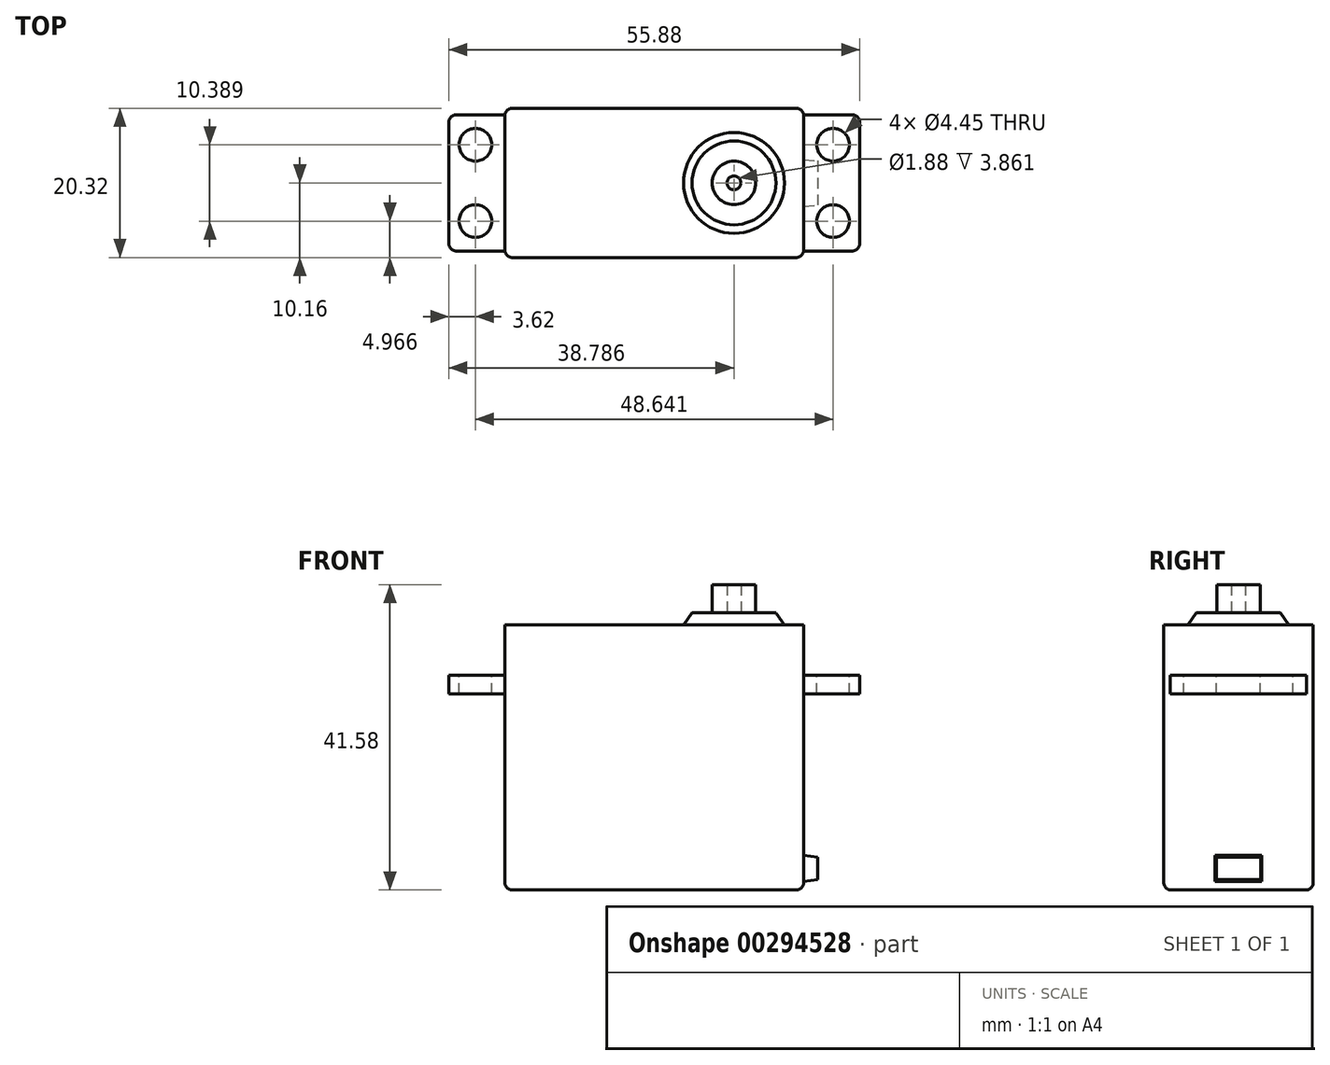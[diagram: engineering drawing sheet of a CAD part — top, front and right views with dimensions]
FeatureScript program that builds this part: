
annotation { "Feature Type Name" : "Feature", "Feature Type Description" : "" }
export const myFeature = defineFeature(function(context is Context, id is Id, definition is map)
    precondition{}
    {
        {
            var Q0;
            Q0=qCreatedBy(makeId("Top.planeOp"),FACE);
            var sketch = newSketch(context, id + "F0", { "sketchPlane" : qUnion([Q0])});
            skLineSegment(sketch, "E0.bottom", {"start": v(20.32, 10.16) * mm, "end": v(-20.32, 10.16) * mm});
            skLineSegment(sketch, "E0.top", {"start": v(20.32, -10.16) * mm, "end": v(-20.32, -10.16) * mm});
            skLineSegment(sketch, "E0.left", {"start": v(20.32, 10.16) * mm, "end": v(20.32, -10.16) * mm});
            skLineSegment(sketch, "E0.right", {"start": v(-20.32, 10.16) * mm, "end": v(-20.32, -10.16) * mm});
            skPoint(sketch, "E0.middle", {"position": v(0, 0) * mm});
            skSolve(sketch);
        }
        {
            var Q0;
            Q0=qSketchRegion(id+"F0",true);
            extrude(context, id + "F1", {"entities" : qUnion([Q0]), "depth" : 36.07 * mm});
        }
        {
            var Q0;
            Q0=makeQuery(id+"F1.opExtrude","SWEPT_FACE",FACE,{"disambiguationData":[OSD([sQuery(id+"F0.wireOp",EDGE,"E0.left")])]});
            var sketch = newSketch(context, id + "F2", { "sketchPlane" : qUnion([Q0])});
            skLineSegment(sketch, "E1.bottom", {"start": v(3.18, 4.75) * mm, "end": v(-3.17, 4.75) * mm});
            skLineSegment(sketch, "E1.top", {"start": v(3.18, 1.14) * mm, "end": v(-3.17, 1.14) * mm});
            skLineSegment(sketch, "E1.left", {"start": v(3.18, 4.75) * mm, "end": v(3.18, 1.14) * mm});
            skLineSegment(sketch, "E1.right", {"start": v(-3.17, 4.75) * mm, "end": v(-3.17, 1.14) * mm});
            skPoint(sketch, "E1.middle", {"position": v(0, 2.95) * mm});
            skSolve(sketch);
        }
        {
            var Q0;
            Q0=makeQuery(id+"F2.imprint","IMPRINT",FACE,{"disambiguationData":[TD([[makeQuery(id+"F2.imprint","IMPRINT",EDGE,{"derivedFrom":sQuery(id+"F2.wireOp",EDGE,"E1.bottom")}),-1.0]])]});
            cPlane(context, id + "F3", {"entities" : qUnion([Q0]), "cplaneType" : CPlaneType.OFFSET, "offset" : 1.9 * mm, "width" : 152.4 * mm, "height" : 152.4 * mm});
        }
        {
            var Q0;
            Q0=qCreatedBy(id+"F3.planeOp",FACE);
            var sketch = newSketch(context, id + "F4", { "sketchPlane" : qUnion([Q0])});
            skPoint(sketch, "E2.0", {"position": v(0, 2.95) * mm});
            skLineSegment(sketch, "E3.bottom", {"start": v(3, 4.48) * mm, "end": v(-3, 4.48) * mm});
            skLineSegment(sketch, "E3.top", {"start": v(3, 1.4) * mm, "end": v(-3, 1.4) * mm});
            skLineSegment(sketch, "E3.left", {"start": v(3, 4.48) * mm, "end": v(3, 1.4) * mm});
            skLineSegment(sketch, "E3.right", {"start": v(-3, 4.48) * mm, "end": v(-3, 1.4) * mm});
            skSolve(sketch);
        }
        {
            var Q1;
            Q1=makeQuery(id+"F2.imprint","IMPRINT",FACE,{"disambiguationData":[TD([[makeQuery(id+"F2.imprint","IMPRINT",EDGE,{"derivedFrom":sQuery(id+"F2.wireOp",EDGE,"E1.bottom")}),1.0]])]});
            var Q2;
            Q2=makeQuery(id+"F4.imprint","IMPRINT",FACE,{"disambiguationData":[TD([[makeQuery(id+"F4.imprint","IMPRINT",EDGE,{"derivedFrom":sQuery(id+"F4.wireOp",EDGE,"E3.bottom")}),1.0]])]});
            loft(context, id + "F5", {"operationType" : NewBodyOperationType.ADD, "sheetProfilesArray" : [{ "sheetProfileEntities" : qUnion([Q1]) }, { "sheetProfileEntities" : qUnion([Q2]) }]});
        }
        {
            var Q0;
            Q0=makeQuery(id+"F1.opExtrude","CAP_FACE",FACE,{"disambiguationData":[OSD([sQuery(id+"F0.wireOp",EDGE,"E0.bottom"),sQuery(id+"F0.wireOp",EDGE,"E0.top"),sQuery(id+"F0.wireOp",EDGE,"E0.left"),sQuery(id+"F0.wireOp",EDGE,"E0.right")])],"isStart":false});
            cPlane(context, id + "F6", {"entities" : qUnion([Q0]), "cplaneType" : CPlaneType.OFFSET, "offset" : 6.86 * mm, "oppositeDirection" : true, "width" : 152.4 * mm, "height" : 152.4 * mm});
        }
        {
            var Q0;
            Q0=qCreatedBy(id+"F6.planeOp",FACE);
            var sketch = newSketch(context, id + "F7", { "sketchPlane" : qUnion([Q0])});
            skLineSegment(sketch, "E4.bottom", {"start": v(-26.92, -9.27) * mm, "end": v(-20.32, -9.27) * mm});
            skLineSegment(sketch, "E4.top", {"start": v(-26.92, 9.27) * mm, "end": v(-20.32, 9.27) * mm});
            skLineSegment(sketch, "E4.left", {"start": v(-27.94, -8.25) * mm, "end": v(-27.94, 8.26) * mm});
            skLineSegment(sketch, "E4.right", {"start": v(-20.32, -9.27) * mm, "end": v(-20.32, 9.27) * mm});
            skPoint(sketch, "E4.middle", {"position": v(-24.13, 0) * mm});
            skLineSegment(sketch, "E5.0", {"start": v(-20.32, 10.16) * mm, "end": v(-20.32, -10.16) * mm});
            skPoint(sketch, "E6.visualSharp", {"position": v(-27.94, -9.27) * mm});
            skArc(sketch, "E6.filletArc", {"start": v(-27.94, -8.25) * mm, "mid": v(-27.64, -8.97) * mm, "end": v(-26.92, -9.27) * mm});
            skPoint(sketch, "E7.visualSharp", {"position": v(-27.94, 9.27) * mm});
            skArc(sketch, "E7.filletArc", {"start": v(-26.92, 9.27) * mm, "mid": v(-27.64, 8.97) * mm, "end": v(-27.94, 8.26) * mm});
            skCircle(sketch, "E8", {"center": v(-24.32, -5.2) * mm, "radius": 2.22 * mm});
            skCircle(sketch, "E9.MirrorC", {"center": v(-24.32, 5.2) * mm, "radius": 2.22 * mm});
            skLineSegment(sketch, "E10.MirrorCS", {"start": v(26.92, 9.27) * mm, "end": v(20.32, 9.27) * mm});
            skArc(sketch, "E11.MirrorCS", {"start": v(26.92, 9.27) * mm, "mid": v(27.64, 8.97) * mm, "end": v(27.94, 8.26) * mm});
            skLineSegment(sketch, "E12.MirrorCS", {"start": v(27.94, -8.25) * mm, "end": v(27.94, 8.26) * mm});
            skArc(sketch, "E13.MirrorCS", {"start": v(27.94, -8.25) * mm, "mid": v(27.64, -8.97) * mm, "end": v(26.92, -9.27) * mm});
            skLineSegment(sketch, "E14.MirrorCS", {"start": v(26.92, -9.27) * mm, "end": v(20.32, -9.27) * mm});
            skCircle(sketch, "E15.MirrorC", {"center": v(24.32, -5.2) * mm, "radius": 2.22 * mm});
            skCircle(sketch, "E16.MirrorC", {"center": v(24.32, 5.2) * mm, "radius": 2.22 * mm});
            skLineSegment(sketch, "E17.MirrorCS", {"start": v(20.32, 10.16) * mm, "end": v(20.32, -10.16) * mm});
            skSolve(sketch);
        }
        {
            var Q0;
            Q0=qSketchRegion(id+"F7",true);
            extrude(context, id + "F8", {"entities" : qUnion([Q0]), "operationType" : NewBodyOperationType.ADD, "oppositeDirection" : true, "depth" : 2.54 * mm});
        }
        {
            var Q0;
            Q0=makeQuery(id+"F1.opExtrude","CAP_FACE",FACE,{"disambiguationData":[OSD([sQuery(id+"F0.wireOp",EDGE,"E0.bottom"),sQuery(id+"F0.wireOp",EDGE,"E0.top"),sQuery(id+"F0.wireOp",EDGE,"E0.left"),sQuery(id+"F0.wireOp",EDGE,"E0.right")])],"isStart":false});
            var sketch = newSketch(context, id + "F9", { "sketchPlane" : qUnion([Q0])});
            skCircle(sketch, "E18", {"center": v(10.85, 0) * mm, "radius": 6.86 * mm});
            skSolve(sketch);
        }
        {
            var Q0;
            Q0=makeQuery(id+"F1.opExtrude","CAP_FACE",FACE,{"disambiguationData":[OSD([sQuery(id+"F0.wireOp",EDGE,"E0.bottom"),sQuery(id+"F0.wireOp",EDGE,"E0.top"),sQuery(id+"F0.wireOp",EDGE,"E0.left"),sQuery(id+"F0.wireOp",EDGE,"E0.right")])],"isStart":false});
            cPlane(context, id + "F10", {"entities" : qUnion([Q0]), "cplaneType" : CPlaneType.OFFSET, "offset" : 1.65 * mm, "width" : 152.4 * mm, "height" : 152.4 * mm});
        }
        {
            var Q0;
            Q0=qCreatedBy(id+"F10.planeOp",FACE);
            var sketch = newSketch(context, id + "F11", { "sketchPlane" : qUnion([Q0])});
            skPoint(sketch, "E19.0", {"position": v(10.85, 0) * mm});
            skCircle(sketch, "E20", {"center": v(10.85, 0) * mm, "radius": 5.7 * mm});
            skSolve(sketch);
        }
        {
            var Q1;
            Q1=makeQuery(id+"F9.imprint","IMPRINT",FACE,{"disambiguationData":[TD([[makeQuery(id+"F9.imprint","IMPRINT",EDGE,{"derivedFrom":sQuery(id+"F9.wireOp",EDGE,"E18")}),1.0]])]});
            var Q2;
            Q2=makeQuery(id+"F11.imprint","IMPRINT",FACE,{"disambiguationData":[TD([[makeQuery(id+"F11.imprint","IMPRINT",EDGE,{"derivedFrom":sQuery(id+"F11.wireOp",EDGE,"E20")}),1.0]])]});
            loft(context, id + "F12", {"operationType" : NewBodyOperationType.ADD, "sheetProfilesArray" : [{ "sheetProfileEntities" : qUnion([Q1]) }, { "sheetProfileEntities" : qUnion([Q2]) }]});
        }
        {
            var Q0;
            Q0=makeQuery(id+"F1.opExtrude","SWEPT_EDGE",EDGE,{"disambiguationData":[OSD([sQuery(id+"F0.wireOp",EDGE,"E0.top"),sQuery(id+"F0.wireOp",EDGE,"E0.left")])]});
            var Q1;
            Q1=makeQuery(id+"F1.opExtrude","SWEPT_EDGE",EDGE,{"disambiguationData":[OSD([sQuery(id+"F0.wireOp",EDGE,"E0.bottom"),sQuery(id+"F0.wireOp",EDGE,"E0.left")])]});
            var Q2;
            Q2=makeQuery(id+"F1.opExtrude","SWEPT_EDGE",EDGE,{"disambiguationData":[OSD([sQuery(id+"F0.wireOp",EDGE,"E0.bottom"),sQuery(id+"F0.wireOp",EDGE,"E0.right")])]});
            var Q3;
            Q3=makeQuery(id+"F1.opExtrude","SWEPT_EDGE",EDGE,{"disambiguationData":[OSD([sQuery(id+"F0.wireOp",EDGE,"E0.top"),sQuery(id+"F0.wireOp",EDGE,"E0.right")])]});
            var Q4;
            Q4=makeQuery(id+"F1.opExtrude","CAP_EDGE",EDGE,{"disambiguationData":[OSD([sQuery(id+"F0.wireOp",EDGE,"E0.top")])],"isStart":true});
            var Q5;
            Q5=makeQuery(id+"F1.opExtrude","CAP_EDGE",EDGE,{"disambiguationData":[OSD([sQuery(id+"F0.wireOp",EDGE,"E0.left")])],"isStart":true});
            var Q6;
            Q6=makeQuery(id+"F1.opExtrude","CAP_EDGE",EDGE,{"disambiguationData":[OSD([sQuery(id+"F0.wireOp",EDGE,"E0.bottom")])],"isStart":true});
            var Q7;
            Q7=makeQuery(id+"F1.opExtrude","CAP_EDGE",EDGE,{"disambiguationData":[OSD([sQuery(id+"F0.wireOp",EDGE,"E0.right")])],"isStart":true});
            fillet(context, id + "F13", {"entities" : qUnion([Q0, Q1, Q2, Q3, Q4, Q5, Q6, Q7]), "radius" : 1.02 * mm, "tangentPropagation" : true, "allowEdgeOverflow" : false});
        }
        {
            var Q0;
            Q0=makeQuery(id+"F12.opLoft","CAP_FACE",FACE,{"disambiguationData":[OSD([makeQuery(id+"F11.imprint","IMPRINT",FACE,{"disambiguationData":[TD([[makeQuery(id+"F11.imprint","IMPRINT",EDGE,{"derivedFrom":sQuery(id+"F11.wireOp",EDGE,"E20")}),1.0]])]})])],"isStart":true});
            var sketch = newSketch(context, id + "F14", { "sketchPlane" : qUnion([Q0])});
            skPoint(sketch, "E21.0", {"position": v(10.85, 0) * mm});
            skCircle(sketch, "E22", {"center": v(10.85, 0) * mm, "radius": 2.95 * mm});
            skCircle(sketch, "E23", {"center": v(10.85, 0) * mm, "radius": 0.94 * mm});
            skSolve(sketch);
        }
        {
            var Q0;
            Q0=qSketchRegion(id+"F14",true);
            extrude(context, id + "F15", {"entities" : qUnion([Q0]), "operationType" : NewBodyOperationType.ADD, "depth" : 3.86 * mm});
        }
    });
